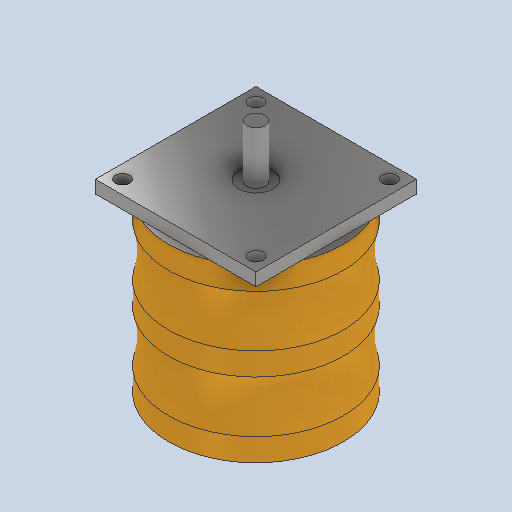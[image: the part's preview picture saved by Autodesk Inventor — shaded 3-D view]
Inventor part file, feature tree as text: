
AUTODESK INVENTOR PART (.ipt)
format: ipt  version: 2023 (Build 270158000, 158)  size: 254,464 bytes
history: native  units: mm
features: sketch x6, extrude x4, other x2, hole x1
ambient origin geometry x8: Origin, YZ Plane, XZ Plane, XY Plane, X Axis, Y Axis, Z Axis, Center Point
bodies: Body1 (feature_tree)
feature tree (13):
  other  "Sólido1"
  extrude  "Extrusão1"  Depth=60.5mm TaperAngle=0.0deg
  extrude  "Extrusão2"  Depth=56.8mm
  hole  "Furo1"  [1 undecoded]
  extrude  "Extrusão3"  Depth=4.5mm
  extrude  "Extrusão4"  Depth=4.8mm
  other  "Revolução1"
  sketch  "Esboço1"  dims[d0=61.75mm d1=60.5mm d2=0.0mm]
  sketch  "Esboço2"  dims[d3=56.8mm d4=56.8mm]
  sketch  "Esboço3"  dims[d5=28.4mm d6=28.4mm]
  sketch  "Esboço4"  dims[d7=4.5mm d8=0.0mm d9=4.8mm]
  sketch  "Esboço5"  dims[d10=4.8mm d11=4.8mm]
  sketch  "Esboço6"  dims[d12=4.8mm d13=4.8mm d14=4.8mm d15=4.8mm d16=4.8mm d17=5.0mm d18=6.0mm d19=6.0mm d20=3.5mm d21=90.0deg d22=0.5mm d23=20.594885mm d24=6.5mm d25=18.0mm d26=0.0mm d27=12.0mm d28=0.5mm d29=0.0mm d32=0.0mm d33=35.0mm d34=0.0mm d35=90.0deg d36=8.0mm d37=8.0mm d40=8.0mm d30=0.5mm d31=0.872665mm]
note: 1 required parameter value undecoded (feature->parameter linkage not recoverable at this tier; creation-order binding heuristic only, values carry confidence <= 0.55)
